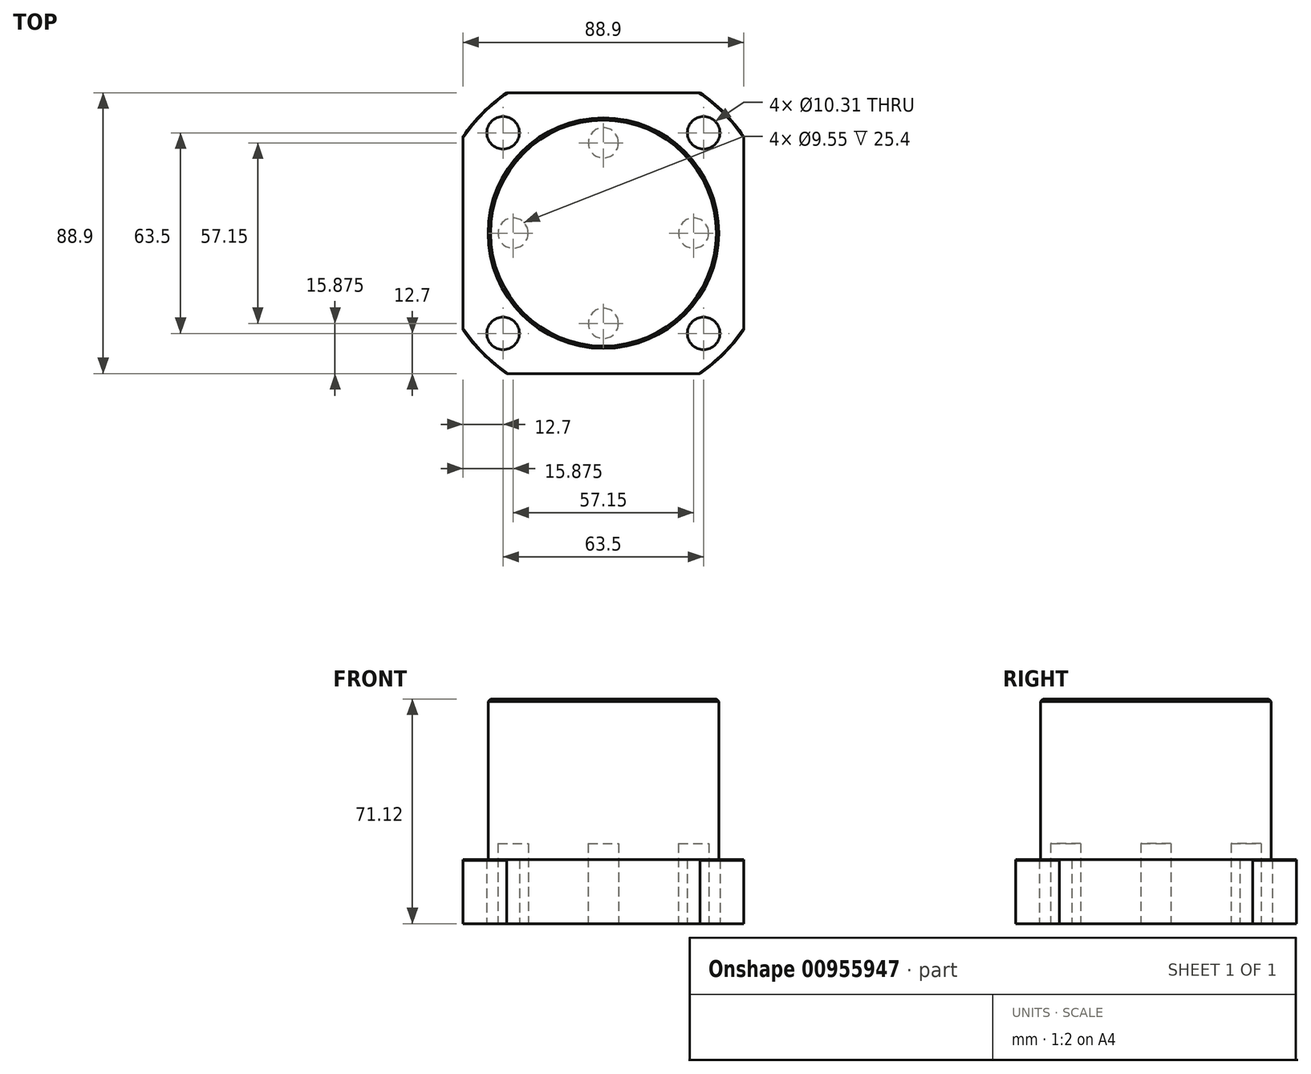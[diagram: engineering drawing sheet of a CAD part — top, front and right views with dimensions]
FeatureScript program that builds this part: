
annotation { "Feature Type Name" : "Feature", "Feature Type Description" : "" }
export const myFeature = defineFeature(function(context is Context, id is Id, definition is map)
    precondition{}
    {
        {
            var Q0;
            Q0=qCreatedBy(makeId("Top.planeOp"),FACE);
            var sketch = newSketch(context, id + "F0", { "sketchPlane" : qUnion([Q0])});
            skCircle(sketch, "E0", {"center": v(0, 0) * mm, "radius": 36.51 * mm});
            skSolve(sketch);
        }
        {
            var Q0;
            Q0 = qSketchRegion(id + "F0", true);
            extrude(context, id + "F1", {"entities" : qUnion([Q0]), "oppositeDirection" : true, "depth" : 50.8 * mm, "offsetDistance" : 25.4 * mm});
        }
        {
            var Q0;
            Q0=makeQuery(id+"F1.opExtrude","CAP_FACE",FACE,{"disambiguationData":[OSD([sQuery(id+"F0.wireOp",EDGE,"E0")])],"isStart":false});
            var sketch = newSketch(context, id + "F2", { "sketchPlane" : qUnion([Q0])});
            skCircle(sketch, "E1", {"center": v(0, 0) * mm, "radius": 53.98 * mm});
            skSolve(sketch);
        }
        {
            var Q0;
            Q0 = qSketchRegion(id + "F2", true);
            extrude(context, id + "F3", {"entities" : qUnion([Q0]), "operationType" : NewBodyOperationType.ADD, "depth" : 20.32 * mm, "offsetDistance" : 25.4 * mm});
        }
        {
            var Q0;
            Q0=makeQuery(id+"F1.opExtrude","CAP_EDGE",EDGE,{"disambiguationData":[OSD([sQuery(id+"F0.wireOp",EDGE,"E0")])],"isStart":true});
            chamfer(context, id + "F4", {"entities" : qUnion([Q0]), "width" : 0.76 * mm, "tangentPropagation" : true});
        }
        {
            var Q0;
            Q0=makeQuery(id+"F3.opExtrude","CAP_EDGE",EDGE,{"disambiguationData":[OSD([sQuery(id+"F2.wireOp",EDGE,"E1")])],"isStart":true});
            chamfer(context, id + "F5", {"entities" : qUnion([Q0]), "width" : 0.25 * mm, "tangentPropagation" : true});
        }
        {
            var Q0;
            Q0=makeQuery(id+"F3.opExtrude","CAP_FACE",FACE,{"disambiguationData":[OSD([sQuery(id+"F2.wireOp",EDGE,"E1")])],"isStart":false});
            var sketch = newSketch(context, id + "F6", { "sketchPlane" : qUnion([Q0])});
            skLineSegment(sketch, "E2.bottom", {"start": v(-44.45, 44.45) * mm, "end": v(44.45, 44.45) * mm});
            skLineSegment(sketch, "E2.top", {"start": v(-44.45, -44.45) * mm, "end": v(44.45, -44.45) * mm});
            skLineSegment(sketch, "E2.left", {"start": v(-44.45, 44.45) * mm, "end": v(-44.45, -44.45) * mm});
            skLineSegment(sketch, "E2.right", {"start": v(44.45, 44.45) * mm, "end": v(44.45, -44.45) * mm});
            skPoint(sketch, "E2.middle", {"position": v(0, 0) * mm});
            skCircle(sketch, "E3", {"center": v(0, 0) * mm, "radius": 69.85 * mm});
            skSolve(sketch);
        }
        {
            var Q0;
            Q0 = qSketchRegion(id + "F6", true);
            extrude(context, id + "F7", {"entities" : qUnion([Q0]), "operationType" : NewBodyOperationType.REMOVE, "oppositeDirection" : true, "depth" : 25.4 * mm, "offsetDistance" : 25.4 * mm});
        }
        {
            var Q0;
            Q0=makeQuery(id+"F3.opExtrude","CAP_FACE",FACE,{"disambiguationData":[OSD([sQuery(id+"F2.wireOp",EDGE,"E1")])],"isStart":false});
            var sketch = newSketch(context, id + "F8", { "sketchPlane" : qUnion([Q0])});
            skCircle(sketch, "E4", {"center": v(-28.58, 0) * mm, "radius": 4.78 * mm});
            skCircle(sketch, "E5", {"center": v(28.58, 0) * mm, "radius": 4.78 * mm});
            skCircle(sketch, "E6", {"center": v(0, 28.58) * mm, "radius": 4.78 * mm});
            skCircle(sketch, "E7", {"center": v(0, -28.58) * mm, "radius": 4.78 * mm});
            skCircle(sketch, "E8", {"center": v(-31.75, 31.75) * mm, "radius": 5.16 * mm});
            skCircle(sketch, "E9", {"center": v(31.75, 31.75) * mm, "radius": 5.16 * mm});
            skCircle(sketch, "E10", {"center": v(31.75, -31.75) * mm, "radius": 5.16 * mm});
            skCircle(sketch, "E11", {"center": v(-31.75, -31.75) * mm, "radius": 5.16 * mm});
            skCircle(sketch, "E12", {"center": v(0, 0) * mm, "radius": 28.58 * mm, "construction": true});
            skSolve(sketch);
        }
        {
            var Q0;
            Q0 = qSketchRegion(id + "F8", true);
            extrude(context, id + "F9", {"entities" : qUnion([Q0]), "operationType" : NewBodyOperationType.REMOVE, "oppositeDirection" : true, "depth" : 25.4 * mm, "offsetDistance" : 25.4 * mm});
        }
    });
